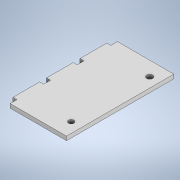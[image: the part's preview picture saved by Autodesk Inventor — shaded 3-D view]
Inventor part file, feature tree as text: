
AUTODESK INVENTOR PART (.ipt)
format: ipt  version: 2022 (Build 260153000, 153)  size: 129,024 bytes
history: native  units: mm
features: extrude x1, sketch x1
ambient origin geometry x8: Origin, YZ Plane, XZ Plane, XY Plane, X Axis, Y Axis, Z Axis, Center Point
bodies: Solid1 (feature_tree)
feature tree (2):
  extrude  "Extrusion1"  Depth=5.0mm
  sketch  "Sketch1"  dims[d1=80.0mm d2=5.0mm d3=3.0mm d4=20.0mm d5=5.0mm d6=20.0mm d7=5.0mm d8=20.0mm d9=3.0mm d10=0.0mm d12=27.0mm d13=32.5mm d14=4.0mm d15=4.0mm d16=54.0mm d17=4.5mm d18=4.5mm d20=5.0mm d21=0.0mm d22=3.0mm d23=0.0mm]
